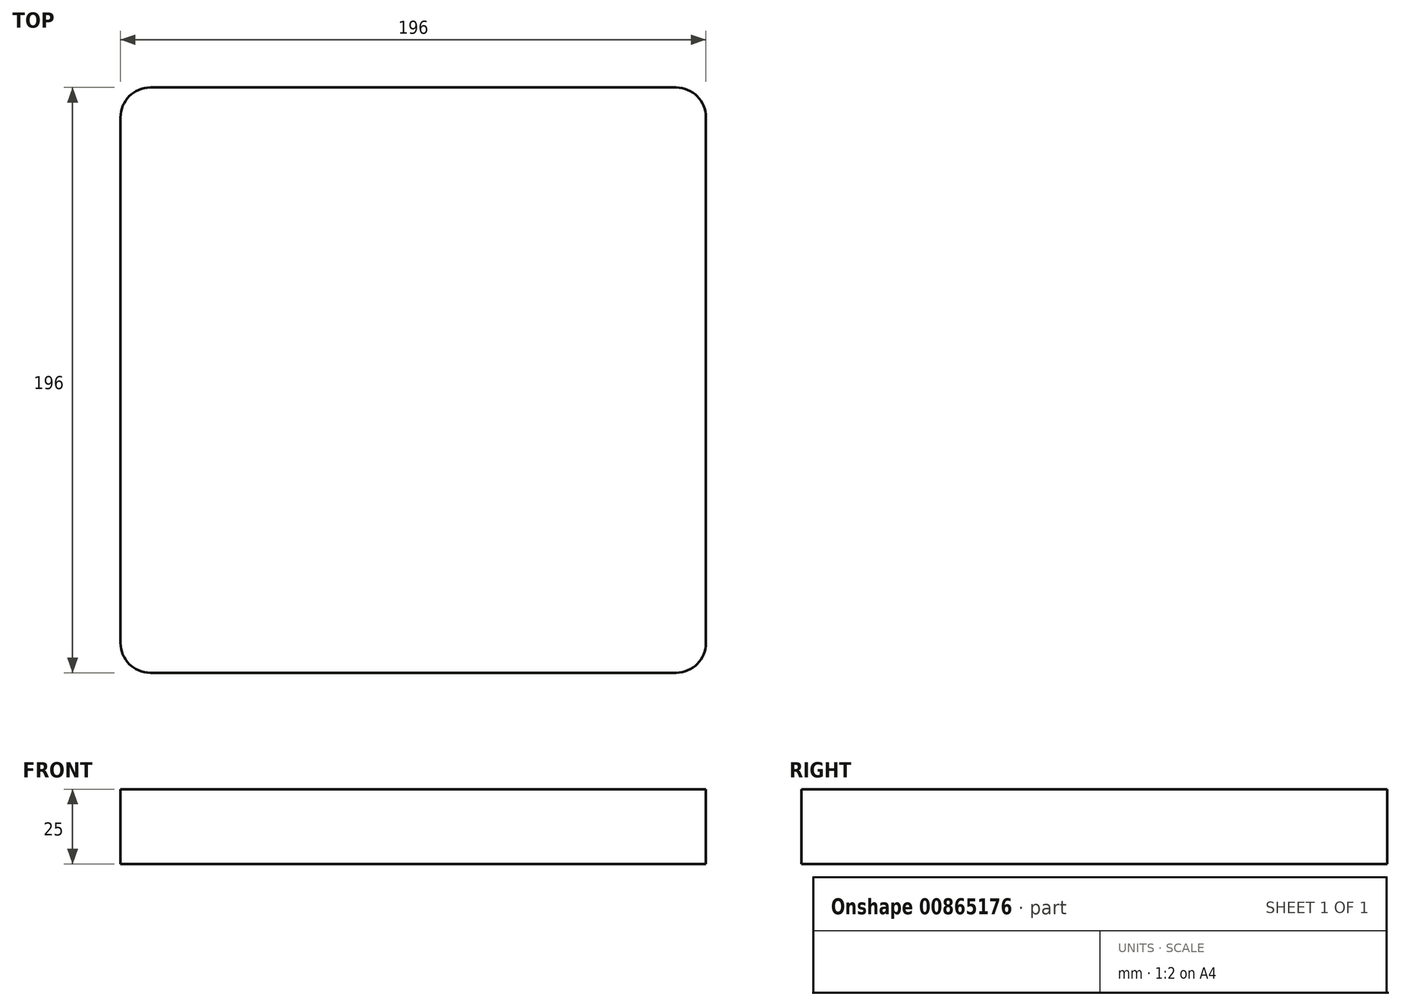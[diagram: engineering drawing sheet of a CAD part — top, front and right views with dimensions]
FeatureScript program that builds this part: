
annotation { "Feature Type Name" : "Feature", "Feature Type Description" : "" }
export const myFeature = defineFeature(function(context is Context, id is Id, definition is map)
    precondition{}
    {
        {
            var Q0;
            Q0=qCreatedBy(makeId("Top.planeOp"),FACE);
            var sketch = newSketch(context, id + "F0", { "sketchPlane" : qUnion([Q0])});
            skLineSegment(sketch, "E0.bottom", {"start": v(-88, 98) * mm, "end": v(88, 98) * mm});
            skLineSegment(sketch, "E0.top", {"start": v(-88, -98) * mm, "end": v(88, -98) * mm});
            skLineSegment(sketch, "E0.left", {"start": v(-98, 88) * mm, "end": v(-98, -88) * mm});
            skLineSegment(sketch, "E0.right", {"start": v(98, 88) * mm, "end": v(98, -88) * mm});
            skPoint(sketch, "E0.middle", {"position": v(0, 0) * mm});
            skPoint(sketch, "E1.visualSharp", {"position": v(-98, 98) * mm});
            skArc(sketch, "E1.filletArc", {"start": v(-88, 98) * mm, "mid": v(-95.07, 95.07) * mm, "end": v(-98, 88) * mm});
            skPoint(sketch, "E2.visualSharp", {"position": v(98, 98) * mm});
            skArc(sketch, "E2.filletArc", {"start": v(98, 88) * mm, "mid": v(95.07, 95.07) * mm, "end": v(88, 98) * mm});
            skPoint(sketch, "E3.visualSharp", {"position": v(98, -98) * mm});
            skArc(sketch, "E3.filletArc", {"start": v(88, -98) * mm, "mid": v(95.07, -95.07) * mm, "end": v(98, -88) * mm});
            skPoint(sketch, "E4.visualSharp", {"position": v(-98, -98) * mm});
            skArc(sketch, "E4.filletArc", {"start": v(-98, -88) * mm, "mid": v(-95.07, -95.07) * mm, "end": v(-88, -98) * mm});
            skSolve(sketch);
        }
        {
            var Q0;
            Q0=makeQuery(id+"F0.imprint","IMPRINT",FACE,{"disambiguationData":[TD([[makeQuery(id+"F0.imprint","IMPRINT",EDGE,{"derivedFrom":sQuery(id+"F0.wireOp",EDGE,"E0.bottom")}),-1.0]])]});
            extrude(context, id + "F1", {"entities" : qUnion([Q0]), "depth" : 25 * mm, "offsetDistance" : 25 * mm});
        }
    });
